# Revit family: IJ-15 inch Drum
name_source: partatom
category: Mechanical Equipment
revit_build: Autodesk Revit 2016 (Build: 20150714_1515(x64)
units: mm (PartAtom-declared; Revit-internal decimal feet)

## family parameters
Always vertical = Yes
Cut with Voids When Loaded = No
OmniClass Number = 23.75.00.00
OmniClass Title = Climate Control (HVAC)
Part Type = Normal
Room Calculation Point = No
Round Connector Dimension = Use Diameter
Shared = No
Work Plane-Based = No

## types (8) — shared parameters
Blade Depth = 6 3/8"
Manufacturer = Anemostat
Model = IJ Infini-Jet Drum Louver
URL = http://www.anemostat.com

## per-type parameters (varying)
| type | Blade Array | D - Drum Depth | Duct Height | Duct Width | Nominal Width | Nominal Width div 2 | Overall Height | Overall Width |
| Model IJ 12" - 20" wide | 7 | 7 27/32" | 15" | 41" | 40" | 20" | 17" | 42 11/16" |
| Model IJ 12" - 25" wide | 4 | 7 5/8" | 12" | 26" | 25" | 12 1/2" | 13 15/16" | 27 11/16" |
| Model IJ 12" - 30" wide | 5 | 7 5/8" | 12" | 31" | 30" | 15" | 13 15/16" | 32 11/16" |
| Model IJ 12" - 35" wide | 6 | 7 5/8" | 12" | 36" | 35" | 17 1/2" | 13 15/16" | 37 11/16" |
| Model IJ 12" - 40" wide | 7 | 7 5/8" | 12" | 41" | 40" | 20" | 13 15/16" | 42 11/16" |
| Model IJ 12" - 50" wide | 9 | 7 5/8" | 12" | 51" | 50" | 25" | 13 15/16" | 52 11/16" |
| Model IJ 12" - 60" wide | 11 | 7 5/8" | 12" | 61" | 60" | 30" | 13 15/16" | 62 11/16" |
| Model IJ 12" - 70" wide | 13 | 7 5/8" | 12" | 71" | 70" | 35" | 13 15/16" | 72 11/16" |

## geometry (parser evidence)
native form markers: Sweep x5
no freeform markers — native parametric forms only
